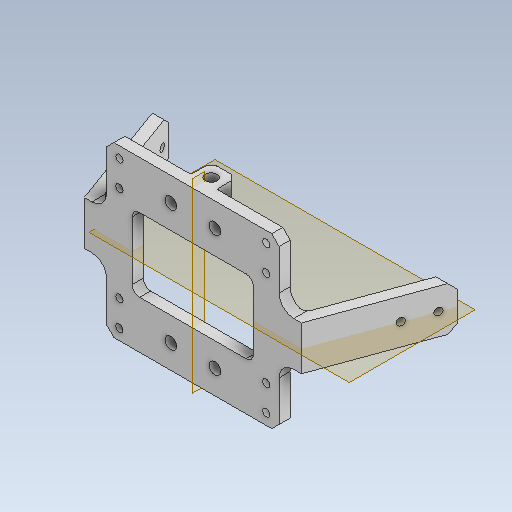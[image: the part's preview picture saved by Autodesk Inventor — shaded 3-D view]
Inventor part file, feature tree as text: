
AUTODESK INVENTOR PART (.ipt)
format: ipt  version: 2023 (Build 270158000, 158)  size: 404,480 bytes
history: native  units: mm
features: other x15, reference x14, sketch x8, extrude x7, projected_geometry x7, fillet x6, mirror x4, chamfer x3, plane x2, hole x1
ambient origin geometry x8: Origin, YZ Plane, XZ Plane, XY Plane, X Axis, Y Axis, Z Axis, Center Point
bodies: Solid1 (feature_tree)
feature tree (67):
  extrude  "Extrusion1"  Depth=12.0mm
  hole  "Hole1"  [1 undecoded]
  plane  "Work Plane1"
  extrude  "Extrusion2"  Depth=19.198622mm
  extrude  "Extrusion3"  Depth=3.0mm TaperAngle=0.0deg
  plane  "Work Plane2"
  extrude  "Extrusion4"  Depth=2.0mm TaperAngle=0.0deg
  mirror  "Mirror1"
  extrude  "Extrusion5"  Depth=6.0mm
  mirror  "Mirror2"
  extrude  "Extrusion6"  Depth=1.0mm
  mirror  "Mirror3"
  chamfer  "Chamfer1"  Distance=6.0mm
  fillet  "Fillet3"  Radius=2.0mm
  fillet  "Fillet4"  Radius=7.0mm
  fillet  "Fillet5"  Radius=7.0mm
  fillet  "Fillet6"  Radius=3.2mm
  fillet  "Fillet7"  Radius=6.0mm
  fillet  "Fillet8"  Radius=1.5mm
  chamfer  "Chamfer2"  Distance=2.0mm
  extrude  "Extrusion7"  Depth=1.0mm
  mirror  "Mirror4"
  chamfer  "Chamfer3"  Distance=2.0mm
  sketch  "Sketch1"  dims[d0=3.0mm d1=0.0mm]
  reference  "Reference1"
  reference  "Reference2"
  reference  "Reference3"
  reference  "Reference4"
  sketch  "Sketch2"  dims[d2=2.0mm d3=6.0mm d4=4.0mm d5=2.0mm d6=90.0deg d7=20.0mm d8=0.0mm d9=12.0mm]
  reference  "Reference5"
  reference  "Reference6"
  reference  "Reference7"
  reference  "Reference8"
  reference  "Reference9"
  reference  "Reference10"
  reference  "Reference11"
  reference  "Reference12"
  sketch  "Sketch3"  dims[d10=8.0mm d11=3.0mm d12=0.0mm]
  projected_geometry  "Projected Loop1"
  sketch  "Sketch4"  dims[d13=30.0mm d14=19.198622mm]
  projected_geometry  "Projected Loop2"
  sketch  "Sketch5"  dims[d15=3.0mm d16=3.0mm d17=0.0mm]
  projected_geometry  "Projected Loop3"
  projected_geometry  "Projected Loop4"
  sketch  "Sketch6"  dims[d19=15.0mm d20=2.0mm d21=0.0mm]
  projected_geometry  "Projected Loop5"
  projected_geometry  "Projected Loop6"
  sketch  "Sketch7"  dims[d23=6.0mm d24=6.0mm]
  projected_geometry  "Projected Loop7"
  sketch  "Sketch8"  dims[d25=3.2mm d26=3.2mm d27=6.0mm d28=0.0mm d29=2.0mm d30=7.0mm d31=7.0mm d32=3.2mm d33=6.0mm d34=0.0mm d35=1.5mm d36=2.0mm d37=45.0deg d38=2.0mm d39=0.5mm d40=2.0mm d41=2.0mm d42=4.0mm d43=1.0mm d44=2.0mm d45=2.0mm d46=45.0deg d47=2.0mm d48=2.0mm d49=6.0mm d50=0.0mm d51=2.0mm d52=2.0mm d53=45.0deg]
  reference  "Reference13"
  reference  "Reference14"
  parser-record x1  (decoder bookkeeping rows leaked as tree rows — omitted from the tree; the rows remain in map.json)
  other  "body_1.iam"
  other  "leg_1_MIR:2"
  other  "reducer_1_MIR:3"
  other  "mot_holder_1_MIR:1"
  other  "leg_1:1"
  other  "reducer_1:3"
  other  "mot_holder_1:1"
  other  "leg_1:2"
  other  "leg_1_MIR:1"
  other  "screw_holder_2_3_MIR:5"
  other  "screw_holder_2_3_MIR:4"
  other  "screw_holder_2_3:14"
  other  "screw_holder_2_3:15"
  other  "body_shell_1:1"
note: 1 required parameter value undecoded (feature->parameter linkage not recoverable at this tier; creation-order binding heuristic only, values carry confidence <= 0.55)
note: 1 file-system path scrubbed to <path> (originals preserved in map.json)
